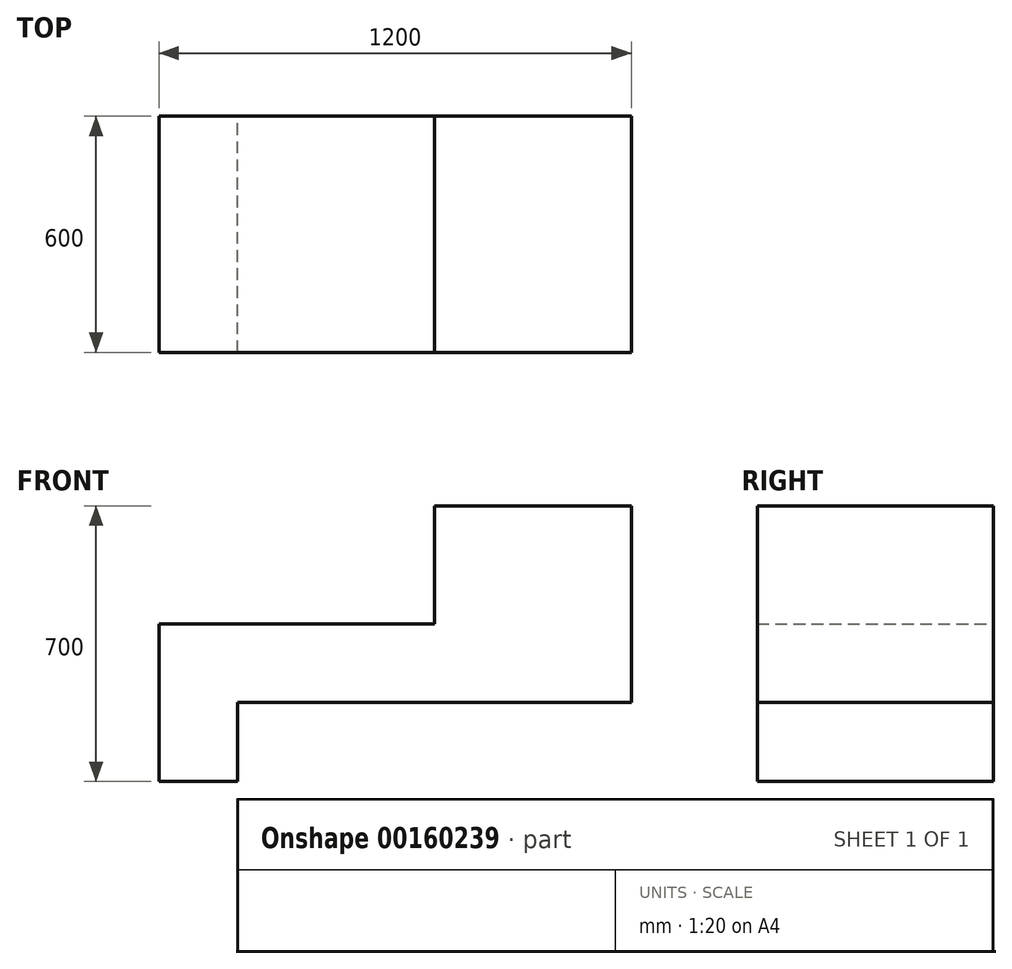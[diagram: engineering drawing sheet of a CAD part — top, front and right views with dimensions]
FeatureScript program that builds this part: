
annotation { "Feature Type Name" : "Feature", "Feature Type Description" : "" }
export const myFeature = defineFeature(function(context is Context, id is Id, definition is map)
    precondition{}
    {
        {
            var Q0;
            Q0=qCreatedBy(makeId("Front.planeOp"),FACE);
            var sketch = newSketch(context, id + "F0", { "sketchPlane" : qUnion([Q0])});
            skLineSegment(sketch, "E0.bottom", {"start": v(-400, -350) * mm, "end": v(-600, -350) * mm});
            skLineSegment(sketch, "E0.top", {"start": v(600, 350) * mm, "end": v(100, 350) * mm});
            skLineSegment(sketch, "E0.left", {"start": v(600, -150) * mm, "end": v(600, 350) * mm});
            skLineSegment(sketch, "E0.right", {"start": v(-600, -350) * mm, "end": v(-600, 50) * mm});
            skPoint(sketch, "E0.middle", {"position": v(0, 0) * mm});
            skLineSegment(sketch, "E1", {"start": v(100, 350) * mm, "end": v(100, 50) * mm});
            skLineSegment(sketch, "E2", {"start": v(100, 50) * mm, "end": v(-600, 50) * mm});
            skLineSegment(sketch, "E3", {"start": v(600, -150) * mm, "end": v(-400, -150) * mm});
            skLineSegment(sketch, "E4", {"start": v(-400, -150) * mm, "end": v(-400, -350) * mm});
            skPoint(sketch, "E5.orphan", {"position": v(-600, 350) * mm});
            skPoint(sketch, "E6.orphan", {"position": v(600, -350) * mm});
            skSolve(sketch);
        }
        {
            var Q0;
            Q0 = qSketchRegion(id + "F0", true);
            extrude(context, id + "F1", {"entities" : qUnion([Q0]), "depth" : 600 * mm});
        }
    });
